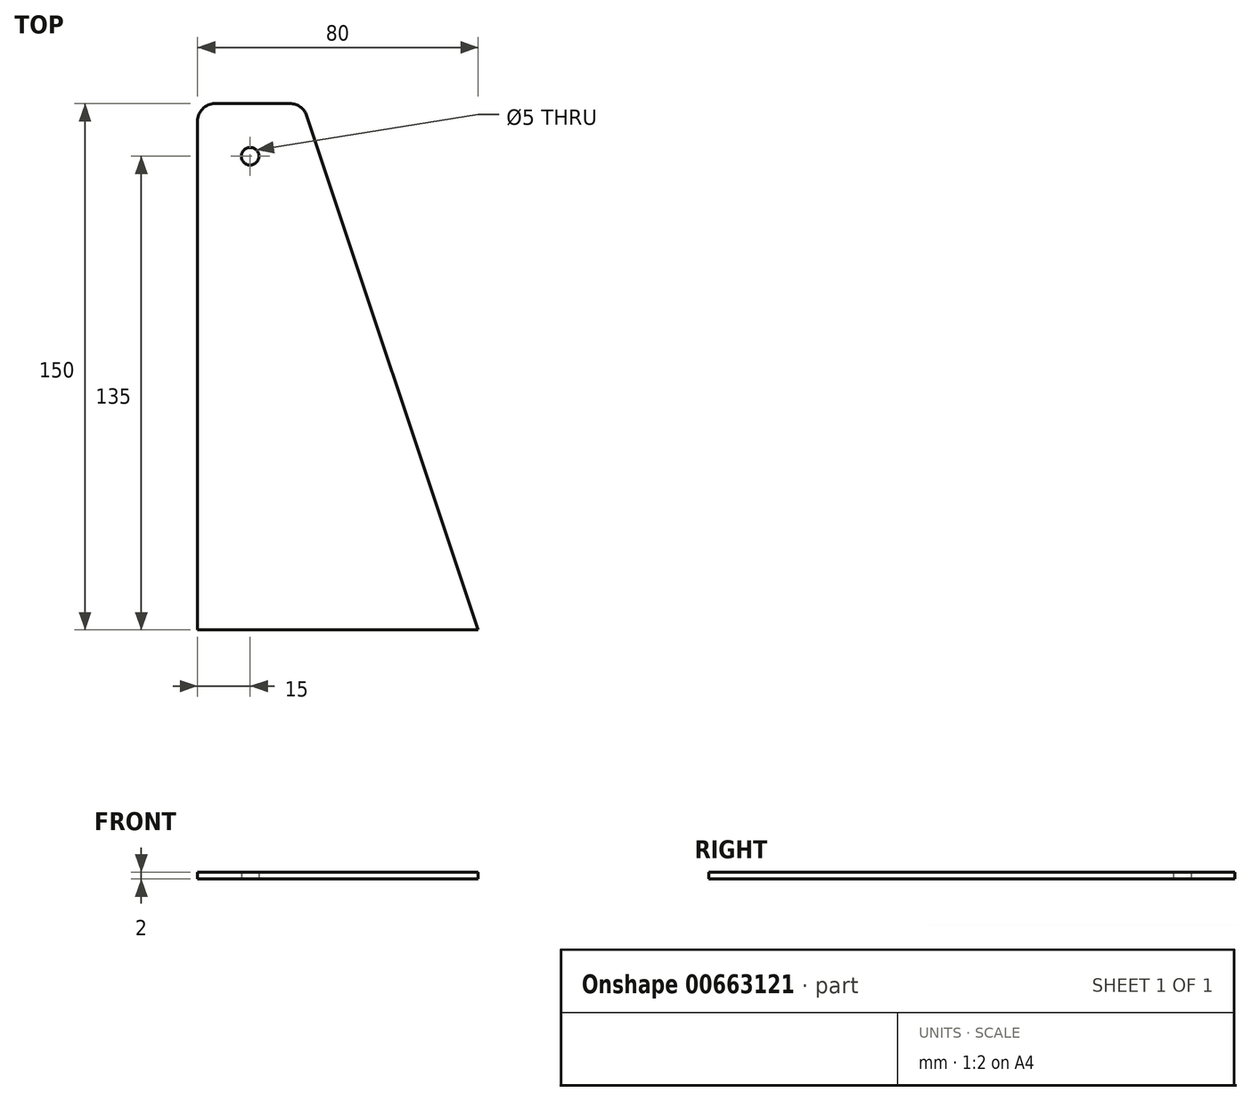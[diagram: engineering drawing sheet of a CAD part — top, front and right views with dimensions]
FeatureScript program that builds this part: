
annotation { "Feature Type Name" : "Feature", "Feature Type Description" : "" }
export const myFeature = defineFeature(function(context is Context, id is Id, definition is map)
    precondition{}
    {
        {
            var Q0;
            Q0=qCreatedBy(makeId("Top.planeOp"),FACE);
            var sketch = newSketch(context, id + "F0", { "sketchPlane" : qUnion([Q0])});
            skLineSegment(sketch, "E0", {"start": v(0, 0) * mm, "end": v(0, 150) * mm});
            skLineSegment(sketch, "E1", {"start": v(0, 150) * mm, "end": v(30, 150) * mm});
            skLineSegment(sketch, "E2", {"start": v(30, 150) * mm, "end": v(80, 0) * mm});
            skLineSegment(sketch, "E3", {"start": v(80, 0) * mm, "end": v(0, 0) * mm});
            skCircle(sketch, "E4", {"center": v(15, 135) * mm, "radius": 2.5 * mm});
            skPoint(sketch, "E4.centerSnap0", {"position": v(15, 150) * mm});
            skSolve(sketch);
        }
        {
            var Q0;
            Q0=makeQuery(id+"F0.imprint","IMPRINT",FACE,{"disambiguationData":[TD([[makeQuery(id+"F0.imprint","IMPRINT",EDGE,{"derivedFrom":sQuery(id+"F0.wireOp",EDGE,"E0")}),-1.0]])]});
            extrude(context, id + "F1", {"entities" : qUnion([Q0]), "depth" : 2 * mm, "offsetDistance" : 25 * mm});
        }
        {
            var Q0;
            Q0=makeQuery(id+"F1.opExtrude","SWEPT_EDGE",EDGE,{"disambiguationData":[OSD([sQuery(id+"F0.wireOp",EDGE,"E0"),sQuery(id+"F0.wireOp",EDGE,"E1")])]});
            var Q1;
            Q1=makeQuery(id+"F1.opExtrude","SWEPT_EDGE",EDGE,{"disambiguationData":[OSD([sQuery(id+"F0.wireOp",EDGE,"E1"),sQuery(id+"F0.wireOp",EDGE,"E2")])]});
            fillet(context, id + "F2", {"entities" : qUnion([Q0, Q1]), "radius" : 5 * mm, "tangentPropagation" : true, "allowEdgeOverflow" : false});
        }
    });
